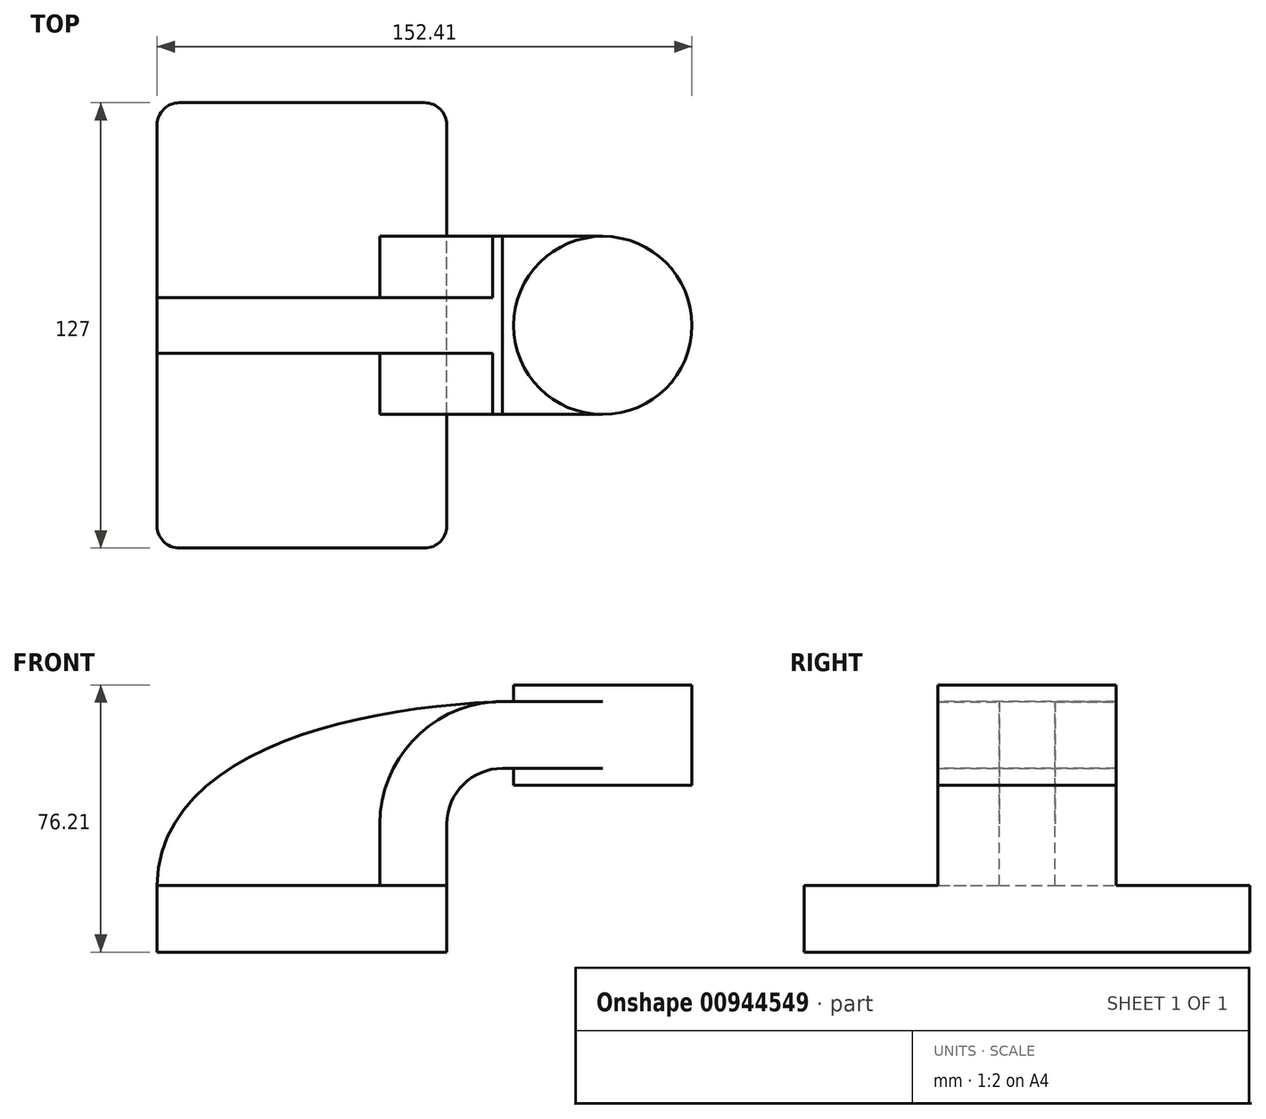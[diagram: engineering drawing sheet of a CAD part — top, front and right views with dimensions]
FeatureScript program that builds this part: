
annotation { "Feature Type Name" : "Feature", "Feature Type Description" : "" }
export const myFeature = defineFeature(function(context is Context, id is Id, definition is map)
    precondition{}
    {
        {
            var Q0;
            Q0=qCreatedBy(makeId("Front.planeOp"),FACE);
            var sketch = newSketch(context, id + "F0", { "sketchPlane" : qUnion([Q0])});
            skLineSegment(sketch, "E0.bottom", {"start": v(41.28, -9.52) * mm, "end": v(-41.28, -9.53) * mm});
            skLineSegment(sketch, "E0.top", {"start": v(41.28, 9.53) * mm, "end": v(-41.28, 9.53) * mm});
            skLineSegment(sketch, "E0.left", {"start": v(41.28, -9.52) * mm, "end": v(41.28, 9.53) * mm});
            skLineSegment(sketch, "E0.right", {"start": v(-41.28, -9.53) * mm, "end": v(-41.28, 9.53) * mm});
            skPoint(sketch, "E0.middle", {"position": v(0, 0) * mm});
            skLineSegment(sketch, "E1.bottom", {"start": v(111.12, 38.1) * mm, "end": v(60.32, 38.1) * mm});
            skLineSegment(sketch, "E1.top", {"start": v(111.12, 66.68) * mm, "end": v(60.32, 66.68) * mm});
            skLineSegment(sketch, "E1.left", {"start": v(111.12, 38.1) * mm, "end": v(111.12, 66.68) * mm});
            skLineSegment(sketch, "E1.right", {"start": v(60.32, 38.1) * mm, "end": v(60.32, 66.68) * mm});
            skPoint(sketch, "E1.middle", {"position": v(85.72, 52.39) * mm});
            skLineSegment(sketch, "E2", {"start": v(41.28, 9.53) * mm, "end": v(41.28, 27) * mm});
            skArc(sketch, "E3", {"start": v(41.27, 27) * mm, "mid": v(45.92, 38.23) * mm, "end": v(57.15, 42.88) * mm});
            skLineSegment(sketch, "E4", {"start": v(57.15, 42.88) * mm, "end": v(85.72, 42.88) * mm});
            skLineSegment(sketch, "E5.0", {"start": v(57.15, 61.93) * mm, "end": v(85.72, 61.93) * mm});
            skArc(sketch, "E5.1", {"start": v(22.23, 27) * mm, "mid": v(32.45, 51.7) * mm, "end": v(57.15, 61.93) * mm});
            skLineSegment(sketch, "E5.2", {"start": v(22.23, 9.53) * mm, "end": v(22.23, 27) * mm});
            skFitSpline(sketch, "E6", {"points": [v(-41.28, 9.53) * mm, v(57.15, 61.93) * mm], "startDerivative": vector(2.22, 118.37) * mm, "endDerivative": vector(117.47, 4.1) * mm});
            skLineSegment(sketch, "E7", {"start": v(85.72, 42.88) * mm, "end": v(85.72, 66.68) * mm});
            skLineSegment(sketch, "E8", {"start": v(85.73, 66.68) * mm, "end": v(85.72, 38.1) * mm});
            skSolve(sketch);
        }
        {
            var Q0;
            Q0=makeQuery(id+"F0.imprint","IMPRINT",FACE,{"disambiguationData":[TD([[makeQuery(id+"F0.imprint","IMPRINT",EDGE,{"derivedFrom":sQuery(id+"F0.wireOp",EDGE,"E0.bottom")}),-1.0]])]});
            extrude(context, id + "F1", {"entities" : qUnion([Q0]), "endBound" : BoundingType.SYMMETRIC, "depth" : 127 * mm, "offsetDistance" : 25.4 * mm});
        }
        {
            var Q0;
            {var subQ1=sQuery(id+"F0.wireOp",EDGE,"E2");Q0=makeQuery(id+"F0.imprint","IMPRINT",FACE,{"disambiguationData":[TD([[makeQuery(id+"F0.imprint","IMPRINT",EDGE,{"derivedFrom":subQ1}),1.0]])]});}
            var Q1;
            {var subQ0=sQuery(id+"F0.wireOp",EDGE,"E4");var subQ1=sQuery(id+"F0.wireOp",EDGE,"E1.right");var subQ2=makeQuery(id+"F0.imprint","INTERSECT",VERTEX,{"derivedFrom":[subQ1,subQ0]});Q1=makeQuery(id+"F0.imprint","IMPRINT",FACE,{"disambiguationData":[TD([[makeQuery(id+"F0.imprint","IMPRINT",EDGE,{"disambiguationData":[TD([[subQ2,-1.0]])],"derivedFrom":subQ1}),-1.0]])]});}
            extrude(context, id + "F2", {"entities" : qUnion([Q0, Q1]), "operationType" : NewBodyOperationType.ADD, "endBound" : BoundingType.SYMMETRIC, "depth" : 50.8 * mm, "offsetDistance" : 25.4 * mm});
        }
        {
            var Q0;
            {var subQ3=sQuery(id+"F0.wireOp",EDGE,"E5.2");Q0=makeQuery(id+"F0.imprint","IMPRINT",FACE,{"disambiguationData":[TD([[makeQuery(id+"F0.imprint","IMPRINT",EDGE,{"derivedFrom":subQ3}),1.0]])]});}
            extrude(context, id + "F3", {"entities" : qUnion([Q0]), "operationType" : NewBodyOperationType.ADD, "endBound" : BoundingType.SYMMETRIC, "depth" : 15.88 * mm, "offsetDistance" : 25.4 * mm});
        }
        {
            var Q0;
            {var subQ4=sQuery(id+"F0.wireOp",EDGE,"E1.left");Q0=makeQuery(id+"F0.imprint","IMPRINT",FACE,{"disambiguationData":[TD([[makeQuery(id+"F0.imprint","IMPRINT",EDGE,{"derivedFrom":subQ4}),1.0]])]});}
            var Q1;
            Q1=sQuery(id+"F0.wireOp",EDGE,"E8");
            revolve(context, id + "F4", {"operationType" : NewBodyOperationType.ADD, "surfaceOperationType" : NewSurfaceOperationType.NEW, "entities" : qUnion([Q0]), "axis" : qUnion([Q1]), "revolveType" : RevolveType.FULL});
        }
        {
            var Q0;
            Q0=makeQuery(id+"F1.opExtrude","CAP_EDGE",EDGE,{"disambiguationData":[OSD([sQuery(id+"F0.wireOp",EDGE,"E0.left")])],"isStart":true});
            var Q1;
            Q1=makeQuery(id+"F1.opExtrude","CAP_EDGE",EDGE,{"disambiguationData":[OSD([sQuery(id+"F0.wireOp",EDGE,"E0.right")])],"isStart":true});
            var Q2;
            Q2=makeQuery(id+"F1.opExtrude","CAP_EDGE",EDGE,{"disambiguationData":[OSD([sQuery(id+"F0.wireOp",EDGE,"E0.right")])],"isStart":false});
            var Q3;
            Q3=makeQuery(id+"F1.opExtrude","CAP_EDGE",EDGE,{"disambiguationData":[OSD([sQuery(id+"F0.wireOp",EDGE,"E0.left")])],"isStart":false});
            fillet(context, id + "F5", {"entities" : qUnion([Q0, Q1, Q2, Q3]), "radius" : 6.35 * mm, "tangentPropagation" : true, "allowEdgeOverflow" : false});
        }
    });
